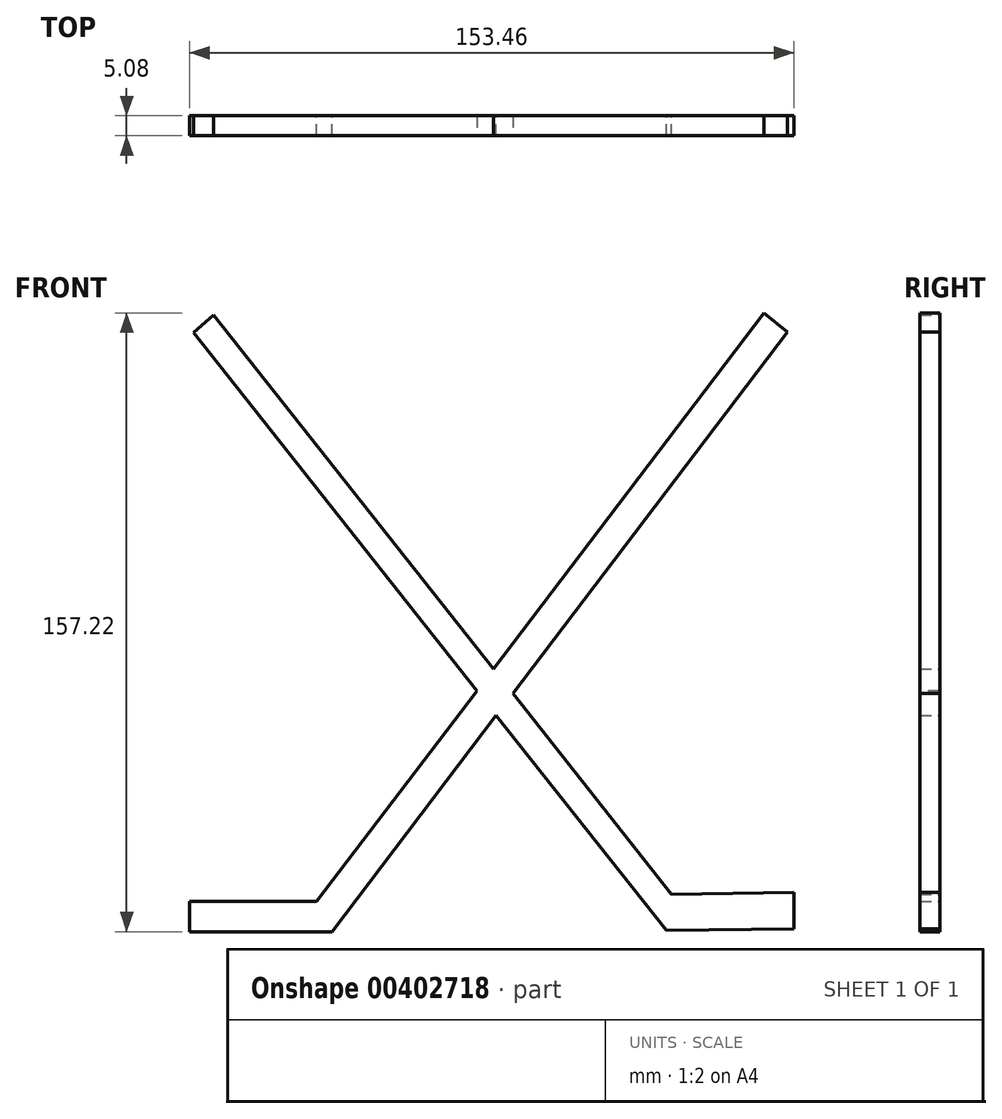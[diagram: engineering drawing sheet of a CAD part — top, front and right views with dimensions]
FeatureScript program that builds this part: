
annotation { "Feature Type Name" : "Feature", "Feature Type Description" : "" }
export const myFeature = defineFeature(function(context is Context, id is Id, definition is map)
    precondition{}
    {
        {
            var Q0;
            Q0=qCreatedBy(makeId("Front.planeOp"),FACE);
            var sketch = newSketch(context, id + "F0", { "sketchPlane" : qUnion([Q0])});
            skLineSegment(sketch, "E0", {"start": v(-75.77, 76.17) * mm, "end": v(44.33, -75.74) * mm});
            skLineSegment(sketch, "E1", {"start": v(76.68, -75.27) * mm, "end": v(44.33, -75.74) * mm});
            skLineSegment(sketch, "E2", {"start": v(76.68, -66.09) * mm, "end": v(76.68, -75.27) * mm});
            skLineSegment(sketch, "E3", {"start": v(76.68, -66.09) * mm, "end": v(45.62, -66.54) * mm});
            skLineSegment(sketch, "E4", {"start": v(45.62, -66.54) * mm, "end": v(-70.72, 80.6) * mm});
            skLineSegment(sketch, "E5", {"start": v(-70.72, 80.6) * mm, "end": v(-75.77, 76.17) * mm});
            skSolve(sketch);
        }
        {
            var Q0;
            Q0 = qSketchRegion(id + "F0", true);
            extrude(context, id + "F1", {"entities" : qUnion([Q0]), "depth" : 5.08 * mm});
        }
        {
            var Q0;
            Q0=qCreatedBy(makeId("Front.planeOp"),FACE);
            var sketch = newSketch(context, id + "F2", { "sketchPlane" : qUnion([Q0])});
            skLineSegment(sketch, "E6", {"start": v(75.1, 76.34) * mm, "end": v(-40.68, -76.03) * mm});
            skLineSegment(sketch, "E7", {"start": v(-40.68, -76.03) * mm, "end": v(-76.78, -76.03) * mm});
            skLineSegment(sketch, "E8", {"start": v(-76.78, -76.03) * mm, "end": v(-76.78, -68.33) * mm});
            skLineSegment(sketch, "E9", {"start": v(-76.78, -68.33) * mm, "end": v(-44.53, -68.33) * mm});
            skLineSegment(sketch, "E10", {"start": v(-44.53, -68.33) * mm, "end": v(69.09, 81.2) * mm});
            skLineSegment(sketch, "E11", {"start": v(69.09, 81.2) * mm, "end": v(75.1, 76.34) * mm});
            skSolve(sketch);
        }
        {
            var Q0;
            Q0 = qSketchRegion(id + "F2", true);
            extrude(context, id + "F3", {"entities" : qUnion([Q0]), "operationType" : NewBodyOperationType.ADD, "depth" : 5.08 * mm});
        }
    });
